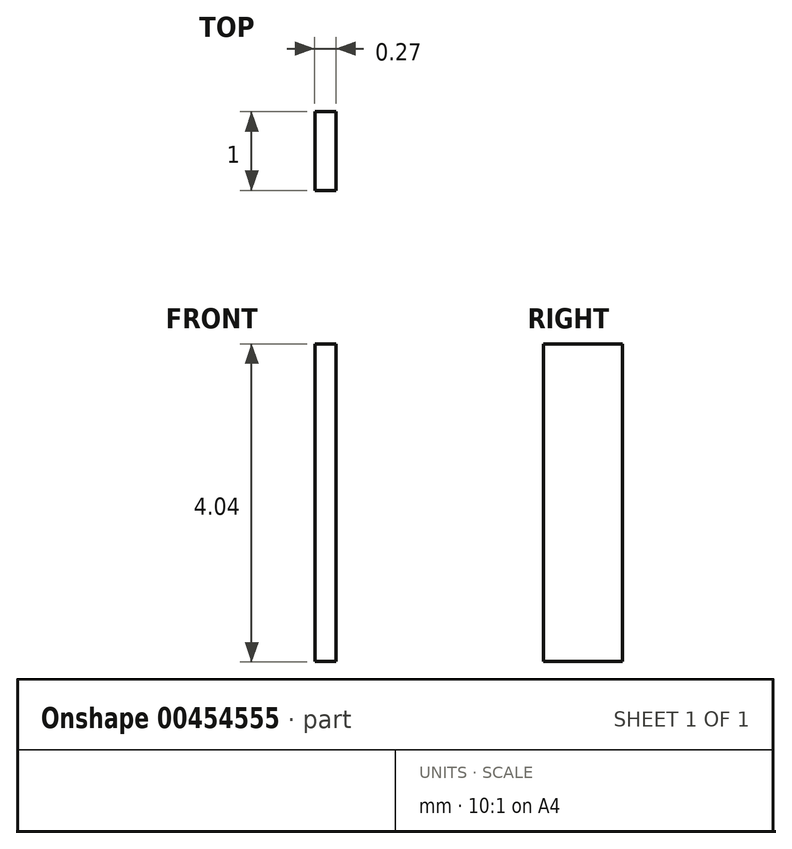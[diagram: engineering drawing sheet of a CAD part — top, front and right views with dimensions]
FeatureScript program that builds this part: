
annotation { "Feature Type Name" : "Feature", "Feature Type Description" : "" }
export const myFeature = defineFeature(function(context is Context, id is Id, definition is map)
    precondition{}
    {
        {
            var Q0;
            Q0=qCreatedBy(makeId("Front.planeOp"),FACE);
            var sketch = newSketch(context, id + "F0", { "sketchPlane" : qUnion([Q0])});
            skLineSegment(sketch, "E0.bottom", {"start": v(0, 0) * mm, "end": v(-74.99, 0) * mm});
            skLineSegment(sketch, "E0.top", {"start": v(0, 55.9) * mm, "end": v(-74.99, 55.9) * mm});
            skLineSegment(sketch, "E0.left", {"start": v(0, 0) * mm, "end": v(0, 55.9) * mm});
            skLineSegment(sketch, "E0.right", {"start": v(-74.99, 0) * mm, "end": v(-74.99, 55.9) * mm});
            skLineSegment(sketch, "E1.bottom", {"start": v(-74.99, 55.9) * mm, "end": v(-75.26, 55.9) * mm});
            skLineSegment(sketch, "E1.top", {"start": v(-74.99, 59.94) * mm, "end": v(-75.26, 59.94) * mm});
            skLineSegment(sketch, "E1.left", {"start": v(-74.99, 55.9) * mm, "end": v(-74.99, 59.94) * mm});
            skLineSegment(sketch, "E1.right", {"start": v(-75.26, 55.9) * mm, "end": v(-75.26, 59.94) * mm});
            skSolve(sketch);
        }
        {
            var Q0;
            Q0 = qSketchRegion(id + "F0", true);
            extrude(context, id + "F1", {"entities" : qUnion([Q0]), "depth" : 1 * mm});
        }
        {
            var Q0;
            Q0=makeQuery(id+"F1.opExtrude","CAP_FACE",FACE,{"disambiguationData":[OSD([sQuery(id+"F0.wireOp",EDGE,"E0.bottom"),sQuery(id+"F0.wireOp",EDGE,"E0.top"),sQuery(id+"F0.wireOp",EDGE,"E0.left"),sQuery(id+"F0.wireOp",EDGE,"E0.right")])],"isStart":true});
            extrude(context, id + "F2", {"entities" : qUnion([Q0]), "operationType" : NewBodyOperationType.REMOVE, "oppositeDirection" : true, "depth" : 74.5 * mm});
        }
    });
